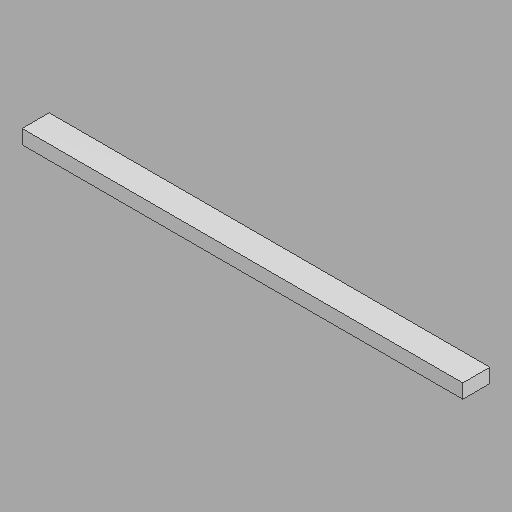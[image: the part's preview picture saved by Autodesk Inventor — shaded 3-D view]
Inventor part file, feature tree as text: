
AUTODESK INVENTOR PART (.ipt)
format: ipt  version: 2022.2 (Build 262287010, 287A)  size: 112,640 bytes
history: native  units: in
note: dims shown in document units (in); Inventor stores cm internally (conversion verified against a paired STEP export)
features: direct_edit x1, other x1, revolve x1
ambient origin geometry x8: Origin, YZ Plane, XZ Plane, XY Plane, X Axis, Y Axis, Z Axis, Center Point
bodies: Solid1 (feature_tree)
feature tree (3):
  direct_edit  "Direct Edit1"
  other  "E125 & E137"
  revolve  "Rotate1"  Angle=90.0deg
